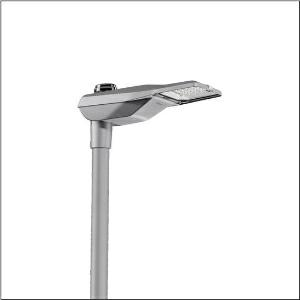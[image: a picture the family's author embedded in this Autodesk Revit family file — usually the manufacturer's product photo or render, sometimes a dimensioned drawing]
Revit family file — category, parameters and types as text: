
# Revit family: streetlight_sl_21_micro___st1_5a_5xe5p37n08db_dfc7
name_source: partatom
category: Lighting Fixtures
units: mm (PartAtom-declared; Revit-internal decimal feet)

## family parameters
Cut with Voids When Loaded = No
Host = Face
Light Source = No
Part Type = Normal
Room Calculation Point = No
Round Connector Dimension = Use Diameter
Shared = No

## types (1)
- --- (1 x LED, 5020 lm, 39.1 W, 3000K)
    Apparent Load = 39 VA
    CIE Flux Codes = 22 53 95 100 100
    Color Rendering = 70
    Color Temperature = 3000K
    Default Elevation = 1800 mm
    Description = Streetlight SL 21 micro, mast luminaire, primary light control with lens, of PMMA, primary optical cover: cover, of toughened safety glass, transparent, light distribution: ST1.5a, light emission: direct distribution, primary light characteristic: asymmetric, installation type: post-top, LED, 3G 1.5mm², High Power LED, rated luminous flux: 5.020lm, luminous efficacy: 128lm/W, light colour: 730, colour temperature: 3000K, control: overheat protection, presetting dimming linear, constant luminous flux control, time-dependent luminous flux control, flexible luminous flux parameterisation, mains connection: 230..240V, AC, 50/60Hz, connection cable pre-assembled, cable length: 6,5m, wiring characteristics: H07RN-F, start of lifetime: 39W, end of service life: 41W, reduction: 18W, luminaire housing, of diecast aluminium (EN AC-44300), powder-coated, Siteco® metallic grey (DB 702S), corrosivity category C5 mid according to DIN EN ISO 12944, multi-level sealing system, sealing non-destructively replaceable, inclination adjustable: 0°, 5°, 10°, 15°, length: 528mm, width: 235mm, height: 110mm, spigot size: 76/60mm (post-top), protection rating (complete): IP66, insulation class (complete): insulation class I (protective earthing), certification: CE, ENEC, ENEC+, VDE, impact resistance: IK09, permissible operating ambient temperature for outdoor applications: -40..+50°C, standard-compliant lighting for roads and squares, packaging unit: 1 piece

Light Distribution: ST1.5a
    Height = 110 mm
    Lamp = 1 x LED
    Lamp Light Flux = 5020 lm
    Lamp Power = 39.1 W
    Lamp count = 1
    Length = 528 mm
    Luminous efficacy = 128 lm/W
    Manufacturer = Siteco
    ModVariant = No
    Model = 5XE5P37N08DB
    Number of Poles = 1
    OnlyDefault = Yes
    Power Factor = 1
    Product Name = Streetlight SL 21 micro | ST1.5a
    Product group = mast luminaire | pylon top
    ProductGroupID = 6100
    Protection Class = Protection class I
    Protection Degree = IP 66
    RLX_Detail_Level = 1
    RLX_Emergency_Light_Flux = 0 lm
    RLX_Emergency_Type = 0
    RLX_Emergency_Type_DB = No
    RlxData = <blob elided: 103093 chars, md5=f9d4cb69>
    Socket = socket
    Standby Power = 0 W
    System Light Flux = 5020 lm
    System Power = 39 W
    Type Comments = factory setting: luminous flux: 100 % | dim-lin: 254 | 765 mA
    Type Image = l_1294375.jpg
    URL = http://relux.com
    VarID = @adj_083143
    Voltage = 0 V
    Weight = 0.00 kg
    Width = 235 mm

## geometry (parser evidence)
native form markers: Blend x4, Sweep x11
no freeform markers — native parametric forms only
